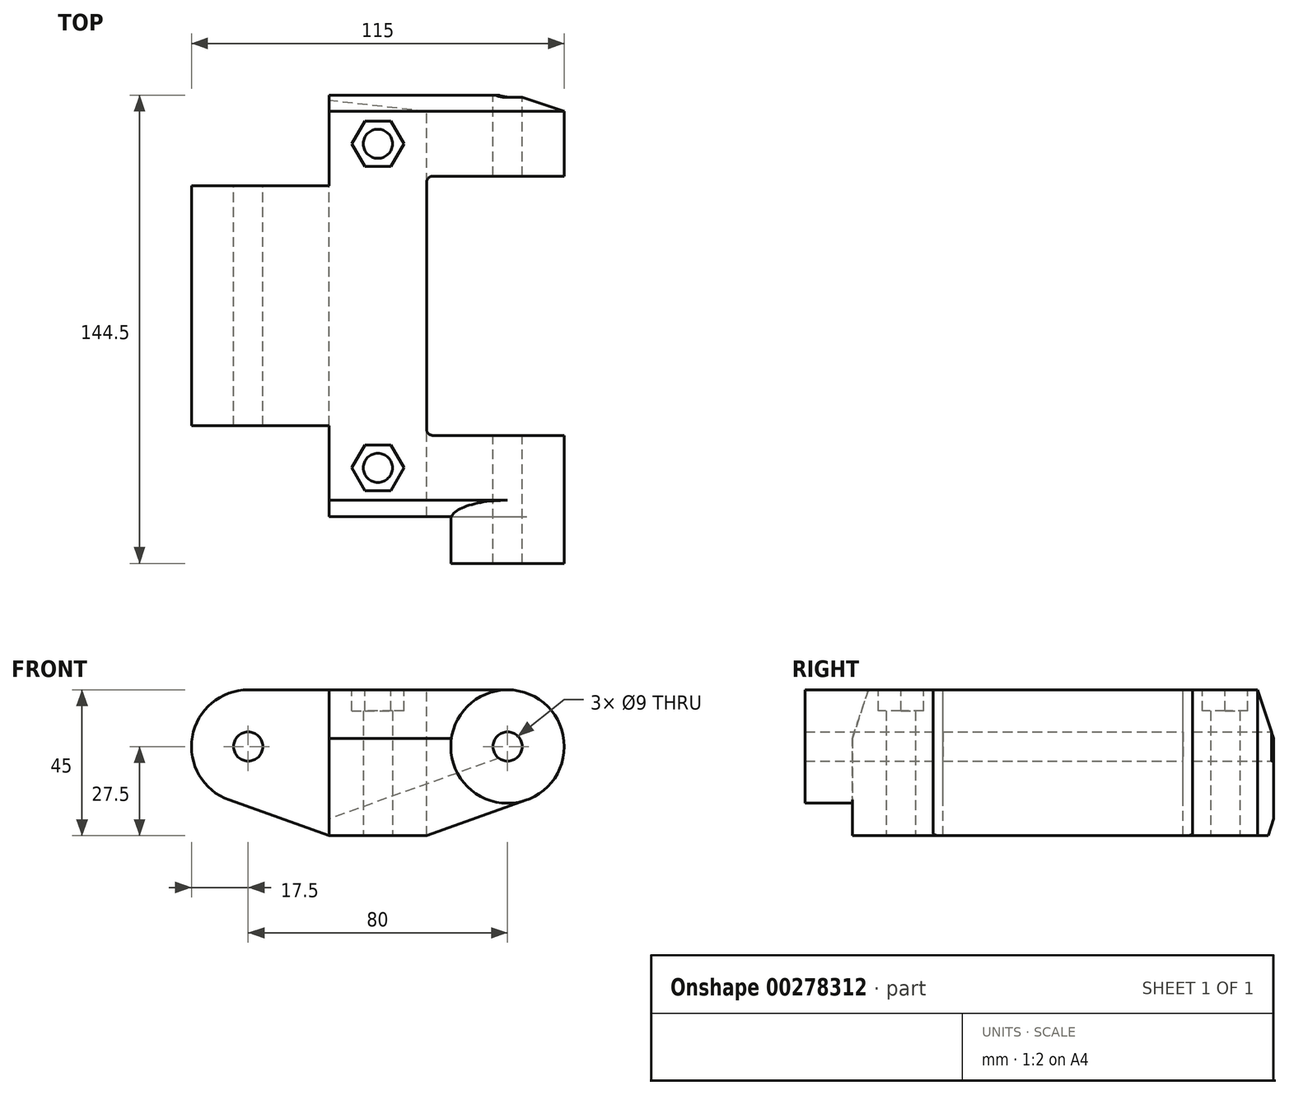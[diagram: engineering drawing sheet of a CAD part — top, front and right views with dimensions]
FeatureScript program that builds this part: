
annotation { "Feature Type Name" : "Feature", "Feature Type Description" : "" }
export const myFeature = defineFeature(function(context is Context, id is Id, definition is map)
    precondition{}
    {
        {
            var Q0;
            Q0=qCreatedBy(makeId("Front.planeOp"),FACE);
            var sketch = newSketch(context, id + "F0", { "sketchPlane" : qUnion([Q0])});
            skArc(sketch, "E0", {"start": v(0, 17.5) * mm, "mid": v(-17.24, 2.98) * mm, "end": v(-5.88, -16.48) * mm});
            skCircle(sketch, "E1", {"center": v(0, 0) * mm, "radius": 4.5 * mm});
            skLineSegment(sketch, "E2", {"start": v(0, 0) * mm, "end": v(80, 0) * mm, "construction": true});
            skCircle(sketch, "E3", {"center": v(80, 0) * mm, "radius": 4.5 * mm});
            skArc(sketch, "E4", {"start": v(85.88, -16.48) * mm, "mid": v(97.24, 2.98) * mm, "end": v(80, 17.5) * mm});
            skLineSegment(sketch, "E5", {"start": v(0, 17.5) * mm, "end": v(80, 17.5) * mm});
            skLineSegment(sketch, "E6", {"start": v(-5.88, -16.48) * mm, "end": v(25, -27.5) * mm});
            skLineSegment(sketch, "E7", {"start": v(25, -27.5) * mm, "end": v(55, -27.5) * mm});
            skLineSegment(sketch, "E8", {"start": v(55, -27.5) * mm, "end": v(85.88, -16.48) * mm});
            skSolve(sketch);
        }
        {
            var Q0;
            Q0=makeQuery(id+"F0.imprint","IMPRINT",FACE,{"disambiguationData":[TD([[makeQuery(id+"F0.imprint","IMPRINT",EDGE,{"derivedFrom":sQuery(id+"F0.wireOp",EDGE,"E0")}),1.0]])]});
            extrude(context, id + "F1", {"entities" : qUnion([Q0]), "endBound" : BoundingType.SYMMETRIC, "depth" : 130 * mm});
        }
        {
            var Q0;
            Q0=makeQuery(id+"F1.opExtrude","SWEPT_FACE",FACE,{"disambiguationData":[OSD([sQuery(id+"F0.wireOp",EDGE,"E5")])]});
            var sketch = newSketch(context, id + "F2", { "sketchPlane" : qUnion([Q0])});
            skLineSegment(sketch, "E9", {"start": v(55, 0) * mm, "end": v(55, 40) * mm});
            skPoint(sketch, "E9.startSnap0", {"position": v(80, 0) * mm});
            skLineSegment(sketch, "E10", {"start": v(110, 40) * mm, "end": v(55, 40) * mm});
            skLineSegment(sketch, "E11", {"start": v(110, 40) * mm, "end": v(110, -40) * mm});
            skLineSegment(sketch, "E12", {"start": v(55, -40) * mm, "end": v(110, -40) * mm});
            skLineSegment(sketch, "E13", {"start": v(55, -40) * mm, "end": v(55, 0) * mm});
            skLineSegment(sketch, "E14.bottom", {"start": v(25, 37) * mm, "end": v(-24.15, 37) * mm});
            skLineSegment(sketch, "E14.top", {"start": v(25, 65) * mm, "end": v(-24.15, 65) * mm});
            skLineSegment(sketch, "E14.left", {"start": v(25, 37) * mm, "end": v(25, 65) * mm});
            skLineSegment(sketch, "E14.right", {"start": v(-24.15, 37) * mm, "end": v(-24.15, 65) * mm});
            skLineSegment(sketch, "E15.bottom", {"start": v(25, -37) * mm, "end": v(-24.15, -37) * mm});
            skLineSegment(sketch, "E15.top", {"start": v(25, -65) * mm, "end": v(-24.15, -65) * mm});
            skLineSegment(sketch, "E15.left", {"start": v(25, -37) * mm, "end": v(25, -65) * mm});
            skLineSegment(sketch, "E15.right", {"start": v(-24.15, -37) * mm, "end": v(-24.15, -65) * mm});
            skSolve(sketch);
        }
        {
            var Q0;
            {var subQ0=sQuery(id+"F2.wireOp",EDGE,"E14.right");Q0=makeQuery(id+"F2.imprint","IMPRINT",FACE,{"disambiguationData":[TD([[makeQuery(id+"F2.imprint","IMPRINT",EDGE,{"derivedFrom":subQ0}),-1.0]])]});}
            var Q1;
            {var subQ0=sQuery(id+"F2.wireOp",EDGE,"E14.left");Q1=makeQuery(id+"F2.imprint","IMPRINT",FACE,{"disambiguationData":[TD([[makeQuery(id+"F2.imprint","IMPRINT",EDGE,{"derivedFrom":subQ0}),1.0]])]});}
            var Q2;
            {var subQ0=sQuery(id+"F2.wireOp",EDGE,"E15.right");Q2=makeQuery(id+"F2.imprint","IMPRINT",FACE,{"disambiguationData":[TD([[makeQuery(id+"F2.imprint","IMPRINT",EDGE,{"derivedFrom":subQ0}),1.0]])]});}
            var Q3;
            {var subQ0=sQuery(id+"F2.wireOp",EDGE,"E15.left");Q3=makeQuery(id+"F2.imprint","IMPRINT",FACE,{"disambiguationData":[TD([[makeQuery(id+"F2.imprint","IMPRINT",EDGE,{"derivedFrom":subQ0}),-1.0]])]});}
            var Q4;
            {var subQ5=sQuery(id+"F2.wireOp",EDGE,"E9");Q4=makeQuery(id+"F2.imprint","IMPRINT",FACE,{"disambiguationData":[TD([[makeQuery(id+"F2.imprint","IMPRINT",EDGE,{"derivedFrom":subQ5}),-1.0]])]});}
            var Q5;
            {var subQ0=sQuery(id+"F2.wireOp",EDGE,"E11");Q5=makeQuery(id+"F2.imprint","IMPRINT",FACE,{"disambiguationData":[TD([[makeQuery(id+"F2.imprint","IMPRINT",EDGE,{"derivedFrom":subQ0}),-1.0]])]});}
            extrude(context, id + "F3", {"entities" : qUnion([Q0, Q1, Q2, Q3, Q4, Q5]), "operationType" : NewBodyOperationType.REMOVE, "endBound" : BoundingType.THROUGH_ALL, "oppositeDirection" : true, "depth" : 25 * mm});
        }
        {
            var Q0;
            Q0=makeQuery(id+"F1.opExtrude","SWEPT_FACE",FACE,{"disambiguationData":[OSD([sQuery(id+"F0.wireOp",EDGE,"E7")])]});
            var sketch = newSketch(context, id + "F4", { "sketchPlane" : qUnion([Q0])});
            skLineSegment(sketch, "E16", {"start": v(40, 65) * mm, "end": v(40, -65) * mm, "construction": true});
            skCircle(sketch, "E17", {"center": v(40, 50) * mm, "radius": 4.5 * mm});
            skCircle(sketch, "E18", {"center": v(40, -50) * mm, "radius": 4.5 * mm});
            skSolve(sketch);
        }
        {
            var Q0;
            Q0=makeQuery(id+"F4.imprint","IMPRINT",FACE,{"disambiguationData":[TD([[makeQuery(id+"F4.imprint","IMPRINT",EDGE,{"derivedFrom":sQuery(id+"F4.wireOp",EDGE,"E17")}),1.0]])]});
            var Q1;
            Q1=makeQuery(id+"F4.imprint","IMPRINT",FACE,{"disambiguationData":[TD([[makeQuery(id+"F4.imprint","IMPRINT",EDGE,{"derivedFrom":sQuery(id+"F4.wireOp",EDGE,"E18")}),1.0]])]});
            extrude(context, id + "F5", {"entities" : qUnion([Q0, Q1]), "operationType" : NewBodyOperationType.REMOVE, "endBound" : BoundingType.THROUGH_ALL, "oppositeDirection" : true, "depth" : 25 * mm});
        }
        {
            var Q0;
            Q0=makeQuery(id+"F1.opExtrude","SWEPT_FACE",FACE,{"disambiguationData":[OSD([sQuery(id+"F0.wireOp",EDGE,"E5")])]});
            var sketch = newSketch(context, id + "F6", { "sketchPlane" : qUnion([Q0])});
            skCircle(sketch, "E19.cCircle", {"center": v(40, 50) * mm, "radius": 7 * mm, "construction": true});
            skLineSegment(sketch, "E19.0", {"start": v(44.04, 43) * mm, "end": v(35.96, 43) * mm});
            skLineSegment(sketch, "E19.1", {"start": v(35.96, 43) * mm, "end": v(31.92, 50) * mm});
            skLineSegment(sketch, "E19.2", {"start": v(31.92, 50) * mm, "end": v(35.96, 57) * mm});
            skLineSegment(sketch, "E19.3", {"start": v(35.96, 57) * mm, "end": v(44.04, 57) * mm});
            skLineSegment(sketch, "E19.4", {"start": v(44.04, 57) * mm, "end": v(48.08, 50) * mm});
            skLineSegment(sketch, "E19.5", {"start": v(48.08, 50) * mm, "end": v(44.04, 43) * mm});
            skPoint(sketch, "E19.0.midPoint", {"position": v(40, 43) * mm});
            skCircle(sketch, "E20.cCircle", {"center": v(40, -50) * mm, "radius": 7 * mm, "construction": true});
            skLineSegment(sketch, "E20.0", {"start": v(48.08, -50) * mm, "end": v(44.04, -57) * mm});
            skLineSegment(sketch, "E20.1", {"start": v(44.04, -57) * mm, "end": v(35.96, -57) * mm});
            skLineSegment(sketch, "E20.2", {"start": v(35.96, -57) * mm, "end": v(31.92, -50) * mm});
            skLineSegment(sketch, "E20.3", {"start": v(31.92, -50) * mm, "end": v(35.96, -43) * mm});
            skLineSegment(sketch, "E20.4", {"start": v(35.96, -43) * mm, "end": v(44.04, -43) * mm});
            skLineSegment(sketch, "E20.5", {"start": v(44.04, -43) * mm, "end": v(48.08, -50) * mm});
            skPoint(sketch, "E20.0.midPoint", {"position": v(46.06, -53.5) * mm});
            skLineSegment(sketch, "E21", {"start": v(40, 50) * mm, "end": v(40, -50) * mm, "construction": true});
            skSolve(sketch);
        }
        {
            var Q0;
            Q0=makeQuery(id+"F6.imprint","IMPRINT",FACE,{"disambiguationData":[TD([[makeQuery(id+"F6.imprint","IMPRINT",EDGE,{"derivedFrom":sQuery(id+"F6.wireOp",EDGE,"E19.0")}),-1.0]])]});
            var Q1;
            Q1=makeQuery(id+"F6.imprint","IMPRINT",FACE,{"disambiguationData":[TD([[makeQuery(id+"F6.imprint","IMPRINT",EDGE,{"derivedFrom":sQuery(id+"F6.wireOp",EDGE,"E20.0")}),-1.0]])]});
            extrude(context, id + "F7", {"entities" : qUnion([Q0, Q1]), "operationType" : NewBodyOperationType.REMOVE, "oppositeDirection" : true, "depth" : 6.5 * mm});
        }
        {
            var Q0;
            Q0=makeQuery(id+"F1.opExtrude","CAP_FACE",FACE,{"disambiguationData":[OSD([sQuery(id+"F0.wireOp",EDGE,"E0"),sQuery(id+"F0.wireOp",EDGE,"E1"),sQuery(id+"F0.wireOp",EDGE,"E3"),sQuery(id+"F0.wireOp",EDGE,"E4"),sQuery(id+"F0.wireOp",EDGE,"E5"),sQuery(id+"F0.wireOp",EDGE,"E6"),sQuery(id+"F0.wireOp",EDGE,"E7"),sQuery(id+"F0.wireOp",EDGE,"E8")])],"isStart":false});
            var sketch = newSketch(context, id + "F8", { "sketchPlane" : qUnion([Q0])});
            skCircle(sketch, "E22", {"center": v(80, 0) * mm, "radius": 4.5 * mm});
            skCircle(sketch, "E23", {"center": v(80, 0) * mm, "radius": 17.5 * mm});
            skSolve(sketch);
        }
        {
            var Q0;
            Q0=makeQuery(id+"F8.imprint","IMPRINT",FACE,{"disambiguationData":[TD([[makeQuery(id+"F8.imprint","IMPRINT",EDGE,{"derivedFrom":sQuery(id+"F8.wireOp",EDGE,"E22")}),-1.0]])]});
            extrude(context, id + "F9", {"entities" : qUnion([Q0]), "operationType" : NewBodyOperationType.ADD, "depth" : 14.5 * mm});
        }
        {
            var Q0;
            Q0=makeQuery(id+"F1.opExtrude","CAP_EDGE",EDGE,{"disambiguationData":[OSD([sQuery(id+"F0.wireOp",EDGE,"E5")])],"isStart":false});
            var Q1;
            Q1=makeQuery(id+"F1.opExtrude","CAP_EDGE",EDGE,{"disambiguationData":[OSD([sQuery(id+"F0.wireOp",EDGE,"E5")])],"isStart":true});
            chamfer(context, id + "F10", {"entities" : qUnion([Q0, Q1]), "chamferType" : ChamferType.TWO_OFFSETS, "width1" : 5 * mm, "oppositeDirection" : false, "width2" : 15 * mm, "tangentPropagation" : true});
        }
        {
            var Q0;
            Q0=makeQuery(id+"F3.boolean.opBoolean","COPY",EDGE,{"derivedFrom":makeQuery(id+"F3.opExtrude","SWEPT_EDGE",EDGE,{"disambiguationData":[OSD([sQuery(id+"F2.wireOp",EDGE,"E12"),sQuery(id+"F2.wireOp",EDGE,"E13")])]})});
            var Q1;
            Q1=makeQuery(id+"F3.boolean.opBoolean","COPY",EDGE,{"derivedFrom":makeQuery(id+"F3.opExtrude","SWEPT_EDGE",EDGE,{"disambiguationData":[OSD([sQuery(id+"F2.wireOp",EDGE,"E9"),sQuery(id+"F2.wireOp",EDGE,"E10")])]})});
            fillet(context, id + "F11", {"entities" : qUnion([Q0, Q1]), "radius" : 2 * mm, "tangentPropagation" : true, "allowEdgeOverflow" : false});
        }
    });
